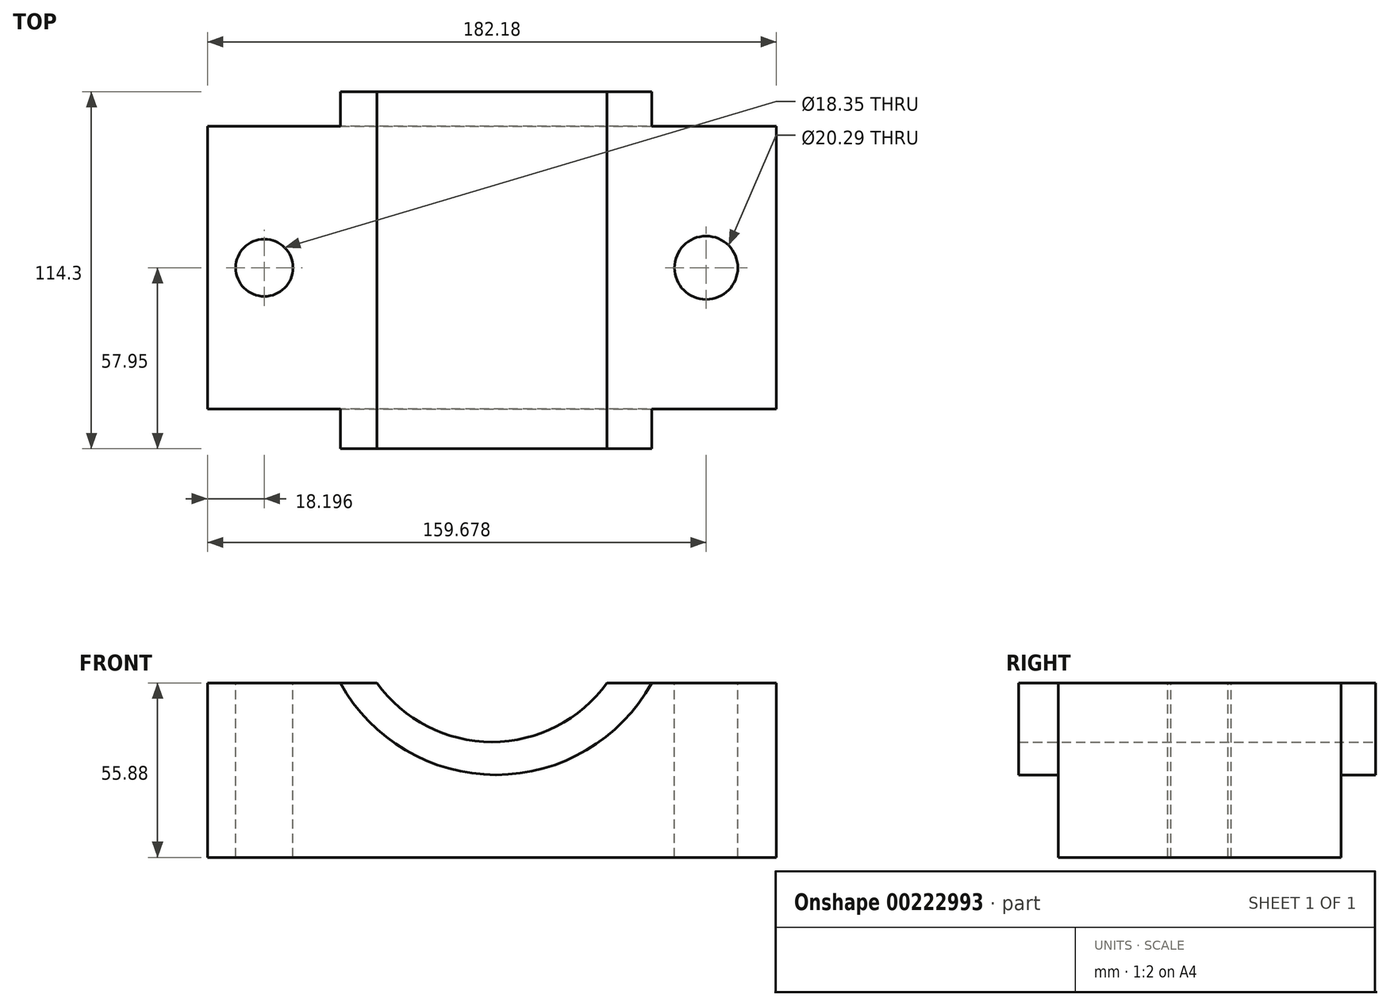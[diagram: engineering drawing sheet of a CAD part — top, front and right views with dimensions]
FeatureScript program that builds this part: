
annotation { "Feature Type Name" : "Feature", "Feature Type Description" : "" }
export const myFeature = defineFeature(function(context is Context, id is Id, definition is map)
    precondition{}
    {
        {
            var Q0;
            Q0=qCreatedBy(makeId("Top.planeOp"),FACE);
            var sketch = newSketch(context, id + "F0", { "sketchPlane" : qUnion([Q0])});
            skLineSegment(sketch, "E0.bottom", {"start": v(91.1, -45.25) * mm, "end": v(-91.1, -45.25) * mm});
            skLineSegment(sketch, "E0.top", {"start": v(91.1, 45.25) * mm, "end": v(-91.1, 45.25) * mm});
            skLineSegment(sketch, "E0.left", {"start": v(91.1, -45.25) * mm, "end": v(91.1, 45.25) * mm});
            skLineSegment(sketch, "E0.right", {"start": v(-91.1, -45.25) * mm, "end": v(-91.1, 45.25) * mm});
            skPoint(sketch, "E0.middle", {"position": v(0, 0) * mm});
            skSolve(sketch);
        }
        {
            var Q0;
            Q0=makeQuery(id+"F0.imprint","IMPRINT",FACE,{"disambiguationData":[TD([[makeQuery(id+"F0.imprint","IMPRINT",EDGE,{"derivedFrom":sQuery(id+"F0.wireOp",EDGE,"E0.bottom")}),-1.0]])]});
            extrude(context, id + "F1", {"entities" : qUnion([Q0]), "depth" : 25.4 * mm});
        }
        {
            var Q0;
            Q0=makeQuery(id+"F1.opExtrude","CAP_FACE",FACE,{"disambiguationData":[OSD([sQuery(id+"F0.wireOp",EDGE,"E0.bottom"),sQuery(id+"F0.wireOp",EDGE,"E0.top"),sQuery(id+"F0.wireOp",EDGE,"E0.left"),sQuery(id+"F0.wireOp",EDGE,"E0.right")])],"isStart":false});
            extrude(context, id + "F2", {"entities" : qUnion([Q0]), "operationType" : NewBodyOperationType.ADD, "depth" : 30.48 * mm});
        }
        {
            var Q0;
            {var subQ0=sQuery(id+"F0.wireOp",EDGE,"E0.bottom");Q0=makeQuery(id+"F2.boolean.opBoolean","MERGE",FACE,{"derivedFrom":[makeQuery(id+"F1.opExtrude","SWEPT_FACE",FACE,{"disambiguationData":[OSD([subQ0])]}),makeQuery(id+"F2.opExtrude","SWEPT_FACE",FACE,{"disambiguationData":[OSD([subQ0])]})]});}
            var sketch = newSketch(context, id + "F3", { "sketchPlane" : qUnion([Q0])});
            skArc(sketch, "E1", {"start": v(-36.84, 55.88) * mm, "mid": v(0, 36.96) * mm, "end": v(36.84, 55.88) * mm});
            skArc(sketch, "E2", {"start": v(-48.56, 55.88) * mm, "mid": v(1.32, 26.43) * mm, "end": v(51.19, 55.88) * mm});
            skSolve(sketch);
        }
        {
            var Q0;
            Q0 = qSketchRegion(id + "F3", true);
            var Q1;
            {var subQ0=sQuery(id+"F3.wireOp",EDGE,"E1");Q1=makeQuery(id+"F3.imprint","IMPRINT",FACE,{"disambiguationData":[TD([[makeQuery(id+"F3.imprint","IMPRINT",EDGE,{"derivedFrom":subQ0}),-1.0]])]});}
            extrude(context, id + "F4", {"entities" : qUnion([Q0, Q1]), "operationType" : NewBodyOperationType.ADD, "depth" : 12.7 * mm, "hasSecondDirection" : true, "secondDirectionOppositeDirection" : true, "secondDirectionDepth" : 101.6 * mm});
        }
        {
            var Q0;
            {var subQ0=sQuery(id+"F0.wireOp",EDGE,"E0.bottom");var subQ1=sQuery(id+"F3.wireOp",EDGE,"E1");Q0=makeQuery(id+"F4.boolean.opBoolean","SPLIT",FACE,{"disambiguationData":[TD([makeQuery(id+"F4.opExtrude","SWEPT_FACE",FACE,{"disambiguationData":[OSD([subQ1])]})])],"derivedFrom":makeQuery(id+"F2.boolean.opBoolean","MERGE",FACE,{"derivedFrom":[makeQuery(id+"F1.opExtrude","SWEPT_FACE",FACE,{"disambiguationData":[OSD([subQ0])]}),makeQuery(id+"F2.opExtrude","SWEPT_FACE",FACE,{"disambiguationData":[OSD([subQ0])]})]})});}
            extrude(context, id + "F5", {"entities" : qUnion([Q0]), "operationType" : NewBodyOperationType.REMOVE, "endBound" : BoundingType.THROUGH_ALL, "oppositeDirection" : true, "depth" : 25.4 * mm});
        }
        {
            var Q0;
            {var subQ1=sQuery(id+"F3.wireOp",EDGE,"E1");var subQ2=sQuery(id+"F0.wireOp",EDGE,"E0.bottom");var subQ3=sQuery(id+"F0.wireOp",EDGE,"E0.right");var subQ4=sQuery(id+"F0.wireOp",EDGE,"E0.top");var subQ5=makeQuery(id+"F2.opExtrude","CAP_EDGE",EDGE,{"disambiguationData":[OSD([subQ2])],"isStart":false});Q0=makeQuery(id+"F5.boolean.opBoolean","SPLIT",FACE,{"disambiguationData":[TD([makeQuery(id+"F1.opExtrude","SWEPT_FACE",FACE,{"disambiguationData":[OSD([subQ3])]})])],"derivedFrom":makeQuery(id+"F4.boolean.opBoolean","MERGE",FACE,{"derivedFrom":[makeQuery(id+"F2.opExtrude","CAP_FACE",FACE,{"disambiguationData":[OSD([subQ2,subQ4,sQuery(id+"F0.wireOp",EDGE,"E0.left"),subQ3])],"isStart":false}),makeQuery(id+"F4.opExtrude","SWEPT_FACE",FACE,{"disambiguationData":[OSD([subQ2]),TDD([makeQuery(id+"F3.imprint","IMPRINT",EDGE,{"disambiguationData":[TD([[makeQuery(id+"F3.imprint","INTERSECT",VERTEX,{"disambiguationData":[OD(0.0)],"derivedFrom":[subQ5,subQ1]}),-1.0]])],"derivedFrom":subQ5})])]}),makeQuery(id+"F4.opExtrude","SWEPT_FACE",FACE,{"disambiguationData":[OSD([subQ2]),TDD([makeQuery(id+"F3.imprint","IMPRINT",EDGE,{"disambiguationData":[TD([[makeQuery(id+"F3.imprint","INTERSECT",VERTEX,{"disambiguationData":[OD(1.0)],"derivedFrom":[subQ5,subQ1]}),1.0]])],"derivedFrom":subQ5})])]})]})});}
            var sketch = newSketch(context, id + "F6", { "sketchPlane" : qUnion([Q0])});
            skCircle(sketch, "E3", {"center": v(-72.9, 0) * mm, "radius": 9.17 * mm});
            skPoint(sketch, "E3.centerSnap0", {"position": v(-91.1, 0) * mm});
            skSolve(sketch);
        }
        {
            var Q0;
            Q0 = qSketchRegion(id + "F6", true);
            extrude(context, id + "F7", {"entities" : qUnion([Q0]), "operationType" : NewBodyOperationType.REMOVE, "endBound" : BoundingType.THROUGH_ALL, "oppositeDirection" : true, "depth" : 25.4 * mm});
        }
        {
            var Q0;
            {var subQ1=sQuery(id+"F3.wireOp",EDGE,"E1");var subQ2=sQuery(id+"F0.wireOp",EDGE,"E0.bottom");var subQ3=sQuery(id+"F0.wireOp",EDGE,"E0.left");var subQ4=sQuery(id+"F0.wireOp",EDGE,"E0.top");var subQ5=makeQuery(id+"F2.opExtrude","CAP_EDGE",EDGE,{"disambiguationData":[OSD([subQ2])],"isStart":false});Q0=makeQuery(id+"F5.boolean.opBoolean","SPLIT",FACE,{"disambiguationData":[TD([makeQuery(id+"F1.opExtrude","SWEPT_FACE",FACE,{"disambiguationData":[OSD([subQ3])]})])],"derivedFrom":makeQuery(id+"F4.boolean.opBoolean","MERGE",FACE,{"derivedFrom":[makeQuery(id+"F2.opExtrude","CAP_FACE",FACE,{"disambiguationData":[OSD([subQ2,subQ4,subQ3,sQuery(id+"F0.wireOp",EDGE,"E0.right")])],"isStart":false}),makeQuery(id+"F4.opExtrude","SWEPT_FACE",FACE,{"disambiguationData":[OSD([subQ2]),TDD([makeQuery(id+"F3.imprint","IMPRINT",EDGE,{"disambiguationData":[TD([[makeQuery(id+"F3.imprint","INTERSECT",VERTEX,{"disambiguationData":[OD(0.0)],"derivedFrom":[subQ5,subQ1]}),-1.0]])],"derivedFrom":subQ5})])]}),makeQuery(id+"F4.opExtrude","SWEPT_FACE",FACE,{"disambiguationData":[OSD([subQ2]),TDD([makeQuery(id+"F3.imprint","IMPRINT",EDGE,{"disambiguationData":[TD([[makeQuery(id+"F3.imprint","INTERSECT",VERTEX,{"disambiguationData":[OD(1.0)],"derivedFrom":[subQ5,subQ1]}),1.0]])],"derivedFrom":subQ5})])]})]})});}
            var sketch = newSketch(context, id + "F8", { "sketchPlane" : qUnion([Q0])});
            skCircle(sketch, "E4", {"center": v(68.59, 0) * mm, "radius": 10.14 * mm});
            skPoint(sketch, "E4.centerSnap0", {"position": v(91.1, 0) * mm});
            skSolve(sketch);
        }
        {
            var Q0;
            Q0 = qSketchRegion(id + "F8", true);
            extrude(context, id + "F9", {"entities" : qUnion([Q0]), "operationType" : NewBodyOperationType.REMOVE, "endBound" : BoundingType.THROUGH_ALL, "oppositeDirection" : true, "depth" : 25.4 * mm});
        }
    });
